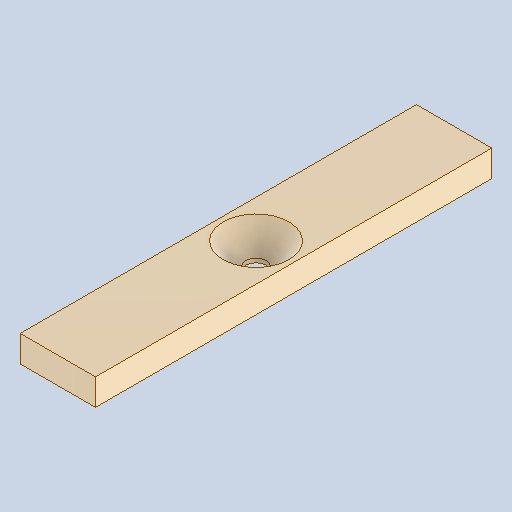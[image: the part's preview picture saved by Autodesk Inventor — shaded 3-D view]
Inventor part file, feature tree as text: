
AUTODESK INVENTOR PART (.ipt)
format: ipt  version: 2025 (Build 290162010, 162A)  size: 112,640 bytes
history: native  units: mm
features: other x3, extrude x1, chamfer x1, sketch x1, reference x1
ambient origin geometry x8: Origin, YZ Plane, XZ Plane, XY Plane, X Axis, Y Axis, Z Axis, Center Point
bodies: Volumenkörper1 (feature_tree)
feature tree (7):
  extrude  "Extrusion1"  Depth=2.0mm TaperAngle=45.0deg
  chamfer  "Fasen1"  [1 undecoded]
  sketch  "Skizze1"  dims[d0=2.0mm d1=0.0mm d2=1.7mm d3=2.0mm d4=45.0deg]
  reference  "Referenz1"
  other  "<userpath>\Documents\Inventor\Krandemonstrator\Demonstrator.iam"
  other  "Demonstrator.iam"
  other  "Katze_Lagerhalter_hinten:1"
note: 1 required parameter value undecoded (feature->parameter linkage not recoverable at this tier; creation-order binding heuristic only, values carry confidence <= 0.55)
